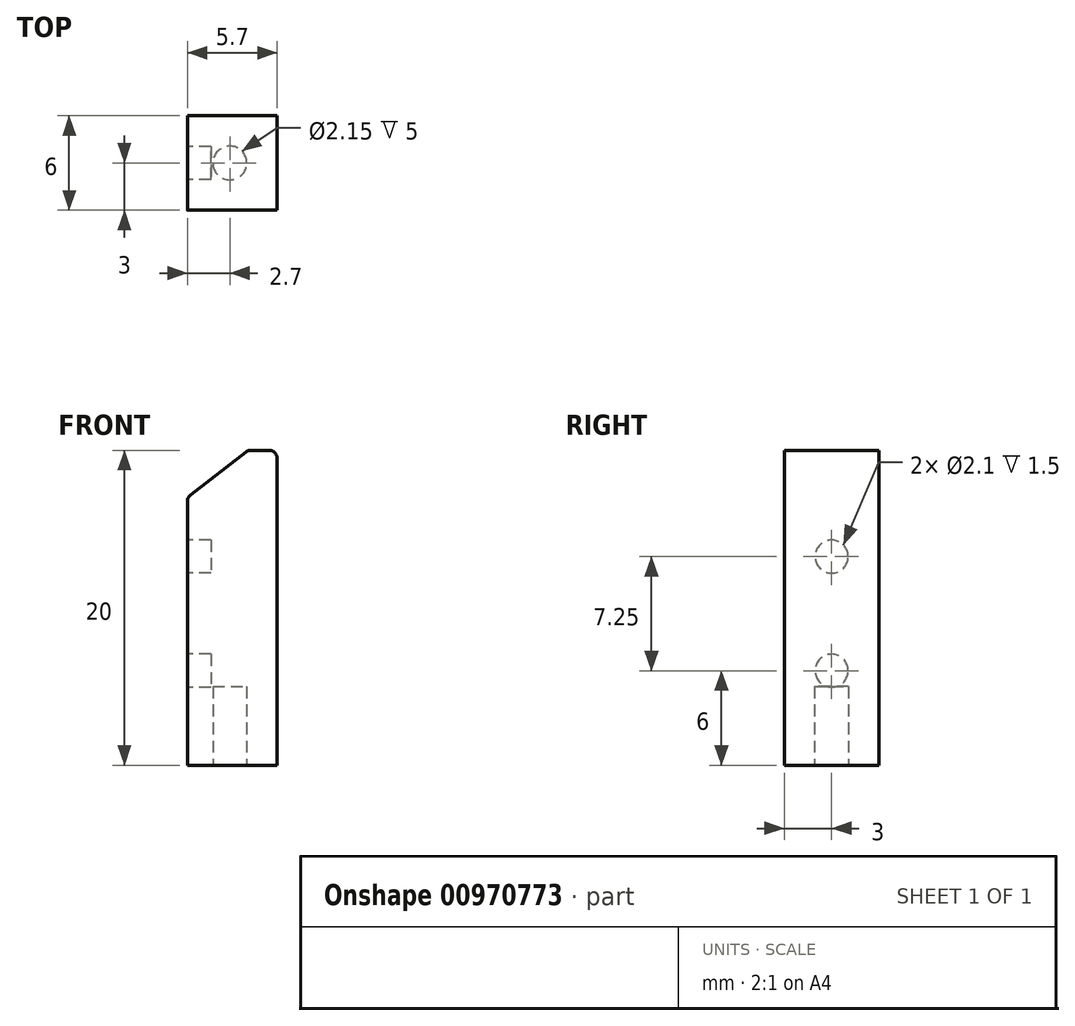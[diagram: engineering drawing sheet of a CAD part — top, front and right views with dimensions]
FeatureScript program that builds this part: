
annotation { "Feature Type Name" : "Feature", "Feature Type Description" : "" }
export const myFeature = defineFeature(function(context is Context, id is Id, definition is map)
    precondition{}
    {
        {
            var Q0;
            Q0=qCreatedBy(makeId("Front.planeOp"),FACE);
            var sketch = newSketch(context, id + "F0", { "sketchPlane" : qUnion([Q0])});
            skLineSegment(sketch, "E0.bottom", {"start": v(2.85, -10) * mm, "end": v(-2.85, -10) * mm});
            skLineSegment(sketch, "E0.top", {"start": v(2.85, 10) * mm, "end": v(1, 10) * mm});
            skLineSegment(sketch, "E0.left", {"start": v(2.85, -10) * mm, "end": v(2.85, 10) * mm});
            skLineSegment(sketch, "E0.right", {"start": v(-2.85, -10) * mm, "end": v(-2.85, 7) * mm});
            skPoint(sketch, "E0.middle", {"position": v(0, 0) * mm});
            skLineSegment(sketch, "E1", {"start": v(1, 10) * mm, "end": v(-2.85, 7) * mm});
            skPoint(sketch, "E2.orphan", {"position": v(-2.85, 10) * mm});
            skSolve(sketch);
        }
        {
            var Q0;
            Q0 = qSketchRegion(id + "F0", true);
            extrude(context, id + "F1", {"entities" : qUnion([Q0]), "depth" : 6 * mm, "offsetDistance" : 25 * mm});
        }
        {
            var Q0;
            Q0=makeQuery(id+"F1.opExtrude","SWEPT_FACE",FACE,{"disambiguationData":[OSD([sQuery(id+"F0.wireOp",EDGE,"E0.right")])]});
            var sketch = newSketch(context, id + "F2", { "sketchPlane" : qUnion([Q0])});
            skLineSegment(sketch, "E3", {"start": v(3, 7) * mm, "end": v(3, -10) * mm, "construction": true});
            skCircle(sketch, "E4", {"center": v(3, -4) * mm, "radius": 1.05 * mm});
            skCircle(sketch, "E5", {"center": v(3, 3.25) * mm, "radius": 1.05 * mm});
            skSolve(sketch);
        }
        {
            var Q0;
            Q0 = qSketchRegion(id + "F2", true);
            extrude(context, id + "F3", {"entities" : qUnion([Q0]), "operationType" : NewBodyOperationType.REMOVE, "oppositeDirection" : true, "depth" : 1.5 * mm, "offsetDistance" : 25 * mm});
        }
        {
            var Q0;
            Q0=makeQuery(id+"F1.opExtrude","SWEPT_FACE",FACE,{"disambiguationData":[OSD([sQuery(id+"F0.wireOp",EDGE,"E0.bottom")])]});
            var sketch = newSketch(context, id + "F4", { "sketchPlane" : qUnion([Q0])});
            skCircle(sketch, "E6", {"center": v(-0.15, 3) * mm, "radius": 1.07 * mm});
            skSolve(sketch);
        }
        {
            var Q0;
            Q0 = qSketchRegion(id + "F4", true);
            extrude(context, id + "F5", {"entities" : qUnion([Q0]), "operationType" : NewBodyOperationType.REMOVE, "oppositeDirection" : true, "depth" : 5 * mm, "offsetDistance" : 25 * mm});
        }
        {
            var Q0;
            Q0=makeQuery(id+"F1.opExtrude","SWEPT_EDGE",EDGE,{"disambiguationData":[OSD([sQuery(id+"F0.wireOp",EDGE,"E0.top"),sQuery(id+"F0.wireOp",EDGE,"E0.left")])]});
            var Q1;
            Q1=makeQuery(id+"F1.opExtrude","SWEPT_EDGE",EDGE,{"disambiguationData":[OSD([sQuery(id+"F0.wireOp",EDGE,"E0.right"),sQuery(id+"F0.wireOp",EDGE,"E1")])]});
            var Q2;
            Q2=makeQuery(id+"F1.opExtrude","SWEPT_EDGE",EDGE,{"disambiguationData":[OSD([sQuery(id+"F0.wireOp",EDGE,"E0.top"),sQuery(id+"F0.wireOp",EDGE,"E1")])]});
            fillet(context, id + "F6", {"entities" : qUnion([Q0, Q1, Q2]), "radius" : .5 * mm, "tangentPropagation" : true, "allowEdgeOverflow" : false});
        }
    });
